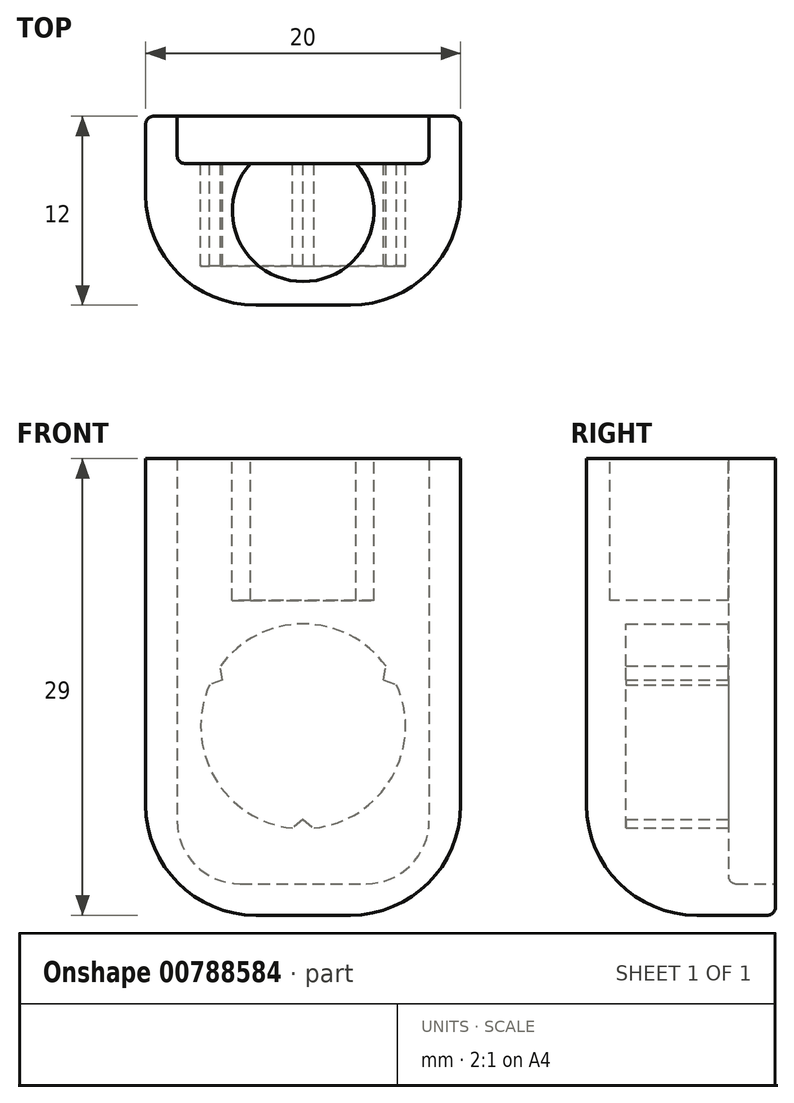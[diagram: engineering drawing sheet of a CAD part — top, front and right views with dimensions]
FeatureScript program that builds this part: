
annotation { "Feature Type Name" : "Feature", "Feature Type Description" : "" }
export const myFeature = defineFeature(function(context is Context, id is Id, definition is map)
    precondition{}
    {
        {
            var Q0;
            Q0=qCreatedBy(makeId("Front.planeOp"),FACE);
            var sketch = newSketch(context, id + "F0", { "sketchPlane" : qUnion([Q0])});
            skLineSegment(sketch, "E0.bottom", {"start": v(10, -14.5) * mm, "end": v(-10, -14.5) * mm});
            skLineSegment(sketch, "E0.top", {"start": v(10, 14.5) * mm, "end": v(-10, 14.5) * mm});
            skLineSegment(sketch, "E0.left", {"start": v(10, -14.5) * mm, "end": v(10, 14.5) * mm});
            skLineSegment(sketch, "E0.right", {"start": v(-10, -14.5) * mm, "end": v(-10, 14.5) * mm});
            skPoint(sketch, "E0.middle", {"position": v(0, 0) * mm});
            skSolve(sketch);
        }
        {
            var Q0;
            Q0=qSketchRegion(id+"F0",true);
            extrude(context, id + "F1", {"entities" : qUnion([Q0]), "flatOperationType" : FlatOperationType.REMOVE, "depth" : 12 * mm, "offsetDistance" : 25 * mm, "domain" : OperationDomain.MODEL});
        }
        {
            var Q0;
            Q0=makeQuery(id+"F0.imprint","IMPRINT",FACE,{"disambiguationData":[TD([[makeQuery(id+"F0.imprint","IMPRINT",EDGE,{"derivedFrom":sQuery(id+"F0.wireOp",EDGE,"E0.bottom")}),-1.0]])]});
            var sketch = newSketch(context, id + "F2", { "sketchPlane" : qUnion([Q0])});
            skLineSegment(sketch, "E1.bottom", {"start": v(-8, 17.5) * mm, "end": v(8, 17.5) * mm});
            skLineSegment(sketch, "E1.top", {"start": v(-8, -12.5) * mm, "end": v(8, -12.5) * mm});
            skLineSegment(sketch, "E1.left", {"start": v(-8, 17.5) * mm, "end": v(-8, -12.5) * mm});
            skLineSegment(sketch, "E1.right", {"start": v(8, 17.5) * mm, "end": v(8, -12.5) * mm});
            skSolve(sketch);
        }
        {
            var Q0;
            Q0=qSketchRegion(id+"F2",true);
            extrude(context, id + "F3", {"entities" : qUnion([Q0]), "operationType" : NewBodyOperationType.REMOVE, "depth" : 3 * mm, "offsetDistance" : 25 * mm});
        }
        {
            var Q0;
            Q0=makeQuery(id+"F3.boolean.opBoolean","COPY",FACE,{"derivedFrom":makeQuery(id+"F3.opExtrude","CAP_FACE",FACE,{"disambiguationData":[OSD([sQuery(id+"F2.wireOp",EDGE,"E1.bottom"),sQuery(id+"F2.wireOp",EDGE,"E1.top"),sQuery(id+"F2.wireOp",EDGE,"E1.left"),sQuery(id+"F2.wireOp",EDGE,"E1.right")])],"isStart":false})});
            var sketch = newSketch(context, id + "F4", { "sketchPlane" : qUnion([Q0])});
            skLineSegment(sketch, "E2", {"start": v(0, -12.5) * mm, "end": v(0, -2.5) * mm, "construction": true});
            skArc(sketch, "E3", {"start": v(0.69, -8.96) * mm, "mid": v(5.63, -5.75) * mm, "end": v(5.94, 0.14) * mm});
            skLineSegment(sketch, "E4", {"start": v(0, -9) * mm, "end": v(0, -8.4) * mm, "construction": true});
            skLineSegment(sketch, "E5", {"start": v(0, -8.4) * mm, "end": v(-0.69, -8.96) * mm});
            skLineSegment(sketch, "E6.MirrorCS", {"start": v(0, -8.4) * mm, "end": v(0.69, -8.96) * mm});
            skLineSegment(sketch, "E7.1.0", {"start": v(5.1, 0.45) * mm, "end": v(5.94, 0.14) * mm});
            skLineSegment(sketch, "E7.1.1", {"start": v(5.1, 0.45) * mm, "end": v(5.25, 1.33) * mm});
            skLineSegment(sketch, "E7.2.0", {"start": v(-5.1, 0.45) * mm, "end": v(-5.25, 1.33) * mm});
            skLineSegment(sketch, "E7.2.1", {"start": v(-5.1, 0.45) * mm, "end": v(-5.94, 0.14) * mm});
            skArc(sketch, "E8.trimOffspring", {"start": v(5.25, 1.33) * mm, "mid": v(0, 4) * mm, "end": v(-5.25, 1.33) * mm});
            skArc(sketch, "E9.trimOffspring", {"start": v(-5.94, 0.14) * mm, "mid": v(-5.45, -6.04) * mm, "end": v(0, -9) * mm});
            skSolve(sketch);
        }
        {
            var Q0;
            Q0=qSketchRegion(id+"F4",true);
            extrude(context, id + "F5", {"entities" : qUnion([Q0]), "operationType" : NewBodyOperationType.REMOVE, "oppositeDirection" : true, "depth" : 6.5 * mm, "offsetDistance" : 25 * mm});
        }
        {
            var Q0;
            Q0=makeQuery(id+"F1.opExtrude","SWEPT_FACE",FACE,{"disambiguationData":[OSD([sQuery(id+"F0.wireOp",EDGE,"E0.top")])]});
            var sketch = newSketch(context, id + "F6", { "sketchPlane" : qUnion([Q0])});
            skLineSegment(sketch, "E10", {"start": v(0, -12) * mm, "end": v(0, -6) * mm, "construction": true});
            skCircle(sketch, "E11", {"center": v(0, -6) * mm, "radius": 4.5 * mm});
            skSolve(sketch);
        }
        {
            var Q0;
            {var subQ0=sQuery(id+"F6.wireOp",EDGE,"E11");var subQ1=makeQuery(id+"F3.boolean.opBoolean","INTERSECT",EDGE,{"derivedFrom":[makeQuery(id+"F1.opExtrude","SWEPT_FACE",FACE,{"disambiguationData":[OSD([sQuery(id+"F0.wireOp",EDGE,"E0.top")])]}),makeQuery(id+"F3.opExtrude","CAP_FACE",FACE,{"disambiguationData":[OSD([sQuery(id+"F2.wireOp",EDGE,"E1.bottom"),sQuery(id+"F2.wireOp",EDGE,"E1.top"),sQuery(id+"F2.wireOp",EDGE,"E1.left"),sQuery(id+"F2.wireOp",EDGE,"E1.right")])],"isStart":false})]});var subQ2=makeQuery(id+"F6.imprint","INTERSECT",VERTEX,{"disambiguationData":[OD(0.0)],"derivedFrom":[subQ1,subQ0]});Q0=makeQuery(id+"F6.imprint","IMPRINT",FACE,{"disambiguationData":[TD([[makeQuery(id+"F6.imprint","IMPRINT",EDGE,{"disambiguationData":[TD([[subQ2,-1.0]])],"derivedFrom":subQ0}),1.0]])]});}
            extrude(context, id + "F7", {"entities" : qUnion([Q0]), "operationType" : NewBodyOperationType.REMOVE, "oppositeDirection" : true, "depth" : 9 * mm, "offsetDistance" : 25 * mm});
        }
        {
            var Q0;
            Q0=makeQuery(id+"F3.boolean.opBoolean","COPY",EDGE,{"derivedFrom":makeQuery(id+"F3.opExtrude","SWEPT_EDGE",EDGE,{"disambiguationData":[OSD([sQuery(id+"F2.wireOp",EDGE,"E1.top"),sQuery(id+"F2.wireOp",EDGE,"E1.right")])]})});
            var Q1;
            Q1=makeQuery(id+"F3.boolean.opBoolean","COPY",EDGE,{"derivedFrom":makeQuery(id+"F3.opExtrude","SWEPT_EDGE",EDGE,{"disambiguationData":[OSD([sQuery(id+"F2.wireOp",EDGE,"E1.top"),sQuery(id+"F2.wireOp",EDGE,"E1.left")])]})});
            fillet(context, id + "F8", {"entities" : qUnion([Q0, Q1]), "radius" : 4 * mm, "tangentPropagation" : true, "allowEdgeOverflow" : false});
        }
        {
            var Q0;
            Q0=makeQuery(id+"F1.opExtrude","SWEPT_EDGE",EDGE,{"disambiguationData":[OSD([sQuery(id+"F0.wireOp",EDGE,"E0.bottom"),sQuery(id+"F0.wireOp",EDGE,"E0.right")])]});
            var Q1;
            Q1=makeQuery(id+"F1.opExtrude","SWEPT_EDGE",EDGE,{"disambiguationData":[OSD([sQuery(id+"F0.wireOp",EDGE,"E0.bottom"),sQuery(id+"F0.wireOp",EDGE,"E0.left")])]});
            var Q2;
            Q2=makeQuery(id+"F1.opExtrude","CAP_EDGE",EDGE,{"disambiguationData":[OSD([sQuery(id+"F0.wireOp",EDGE,"E0.bottom")])],"isStart":false});
            var Q3;
            Q3=makeQuery(id+"F1.opExtrude","CAP_EDGE",EDGE,{"disambiguationData":[OSD([sQuery(id+"F0.wireOp",EDGE,"E0.left")])],"isStart":false});
            var Q4;
            Q4=makeQuery(id+"F1.opExtrude","CAP_EDGE",EDGE,{"disambiguationData":[OSD([sQuery(id+"F0.wireOp",EDGE,"E0.right")])],"isStart":false});
            fillet(context, id + "F9", {"entities" : qUnion([Q0, Q1, Q2, Q3, Q4]), "radius" : 7 * mm, "tangentPropagation" : true, "allowEdgeOverflow" : false});
        }
        {
            var Q0;
            Q0=makeQuery(id+"F3.boolean.opBoolean","COPY",EDGE,{"derivedFrom":makeQuery(id+"F3.opExtrude","CAP_EDGE",EDGE,{"disambiguationData":[OSD([sQuery(id+"F2.wireOp",EDGE,"E1.right")])],"isStart":false})});
            var Q1;
            Q1=makeQuery(id+"F1.opExtrude","CAP_EDGE",EDGE,{"disambiguationData":[OSD([sQuery(id+"F0.wireOp",EDGE,"E0.left")])],"isStart":true});
            fillet(context, id + "F10", {"entities" : qUnion([Q0, Q1]), "radius" : 0.5 * mm, "tangentPropagation" : true, "allowEdgeOverflow" : false});
        }
    });
